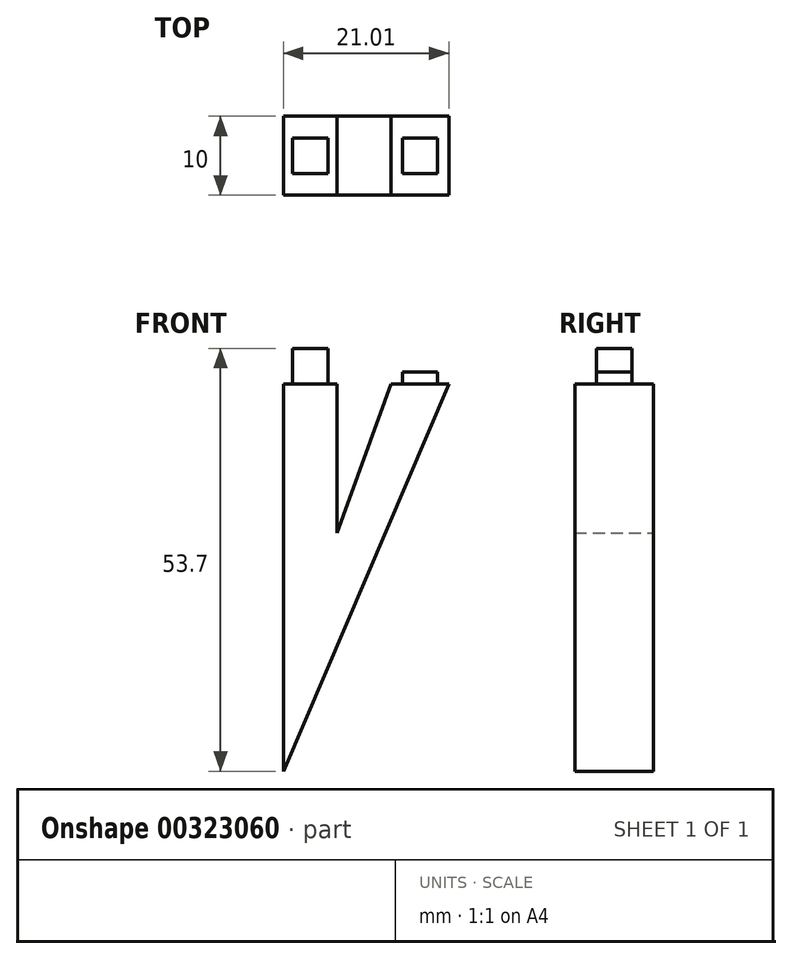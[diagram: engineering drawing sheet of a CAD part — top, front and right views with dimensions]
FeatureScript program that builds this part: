
annotation { "Feature Type Name" : "Feature", "Feature Type Description" : "" }
export const myFeature = defineFeature(function(context is Context, id is Id, definition is map)
    precondition{}
    {
        {
            var Q0;
            Q0=qCreatedBy(makeId("Front.planeOp"),FACE);
            var sketch = newSketch(context, id + "F0", { "sketchPlane" : qUnion([Q0])});
            skLineSegment(sketch, "E0", {"start": v(0, 0) * mm, "end": v(0, -49.2) * mm});
            skLineSegment(sketch, "E1", {"start": v(0, -49.2) * mm, "end": v(21.01, 0) * mm});
            skLineSegment(sketch, "E2", {"start": v(0, 0) * mm, "end": v(6.8, 0) * mm});
            skLineSegment(sketch, "E3", {"start": v(21.01, 0) * mm, "end": v(13.67, 0) * mm});
            skLineSegment(sketch, "E4", {"start": v(6.8, 0) * mm, "end": v(6.8, -18.95) * mm});
            skLineSegment(sketch, "E5", {"start": v(6.8, -18.95) * mm, "end": v(13.67, 0) * mm});
            skSolve(sketch);
        }
        {
            var Q0;
            Q0=makeQuery(id+"F0.imprint","IMPRINT",FACE,{"disambiguationData":[TD([[makeQuery(id+"F0.imprint","IMPRINT",EDGE,{"derivedFrom":sQuery(id+"F0.wireOp",EDGE,"E0")}),1.0]])]});
            extrude(context, id + "F1", {"entities" : qUnion([Q0]), "depth" : 10 * mm});
        }
        {
            var Q0;
            Q0=makeQuery(id+"F1.opExtrude","SWEPT_FACE",FACE,{"disambiguationData":[OSD([sQuery(id+"F0.wireOp",EDGE,"E2")])]});
            var sketch = newSketch(context, id + "F2", { "sketchPlane" : qUnion([Q0])});
            skLineSegment(sketch, "E6.bottom", {"start": v(5.65, -7.25) * mm, "end": v(1.15, -7.25) * mm});
            skLineSegment(sketch, "E6.top", {"start": v(5.65, -2.75) * mm, "end": v(1.15, -2.75) * mm});
            skLineSegment(sketch, "E6.left", {"start": v(5.65, -7.25) * mm, "end": v(5.65, -2.75) * mm});
            skLineSegment(sketch, "E6.right", {"start": v(1.15, -7.25) * mm, "end": v(1.15, -2.75) * mm});
            skPoint(sketch, "E6.middle", {"position": v(3.4, -5) * mm});
            skSolve(sketch);
        }
        {
            var Q0;
            Q0=makeQuery(id+"F2.imprint","IMPRINT",FACE,{"disambiguationData":[TD([[makeQuery(id+"F2.imprint","IMPRINT",EDGE,{"derivedFrom":sQuery(id+"F2.wireOp",EDGE,"E6.bottom")}),-1.0]])]});
            extrude(context, id + "F3", {"entities" : qUnion([Q0]), "operationType" : NewBodyOperationType.ADD, "depth" : 4.5 * mm});
        }
        {
            var Q0;
            Q0=makeQuery(id+"F1.opExtrude","SWEPT_FACE",FACE,{"disambiguationData":[OSD([sQuery(id+"F0.wireOp",EDGE,"E3")])]});
            var sketch = newSketch(context, id + "F4", { "sketchPlane" : qUnion([Q0])});
            skLineSegment(sketch, "E7.bottom", {"start": v(19.6, -7.25) * mm, "end": v(15.1, -7.25) * mm});
            skLineSegment(sketch, "E7.top", {"start": v(19.6, -2.75) * mm, "end": v(15.1, -2.75) * mm});
            skLineSegment(sketch, "E7.left", {"start": v(19.6, -7.25) * mm, "end": v(19.6, -2.75) * mm});
            skLineSegment(sketch, "E7.right", {"start": v(15.1, -7.25) * mm, "end": v(15.1, -2.75) * mm});
            skPoint(sketch, "E7.middle", {"position": v(17.34, -5) * mm});
            skSolve(sketch);
        }
        {
            var Q0;
            Q0=makeQuery(id+"F4.imprint","IMPRINT",FACE,{"disambiguationData":[TD([[makeQuery(id+"F4.imprint","IMPRINT",EDGE,{"derivedFrom":sQuery(id+"F4.wireOp",EDGE,"E7.bottom")}),-1.0]])]});
            extrude(context, id + "F5", {"entities" : qUnion([Q0]), "operationType" : NewBodyOperationType.ADD, "depth" : 1.5 * mm});
        }
    });
